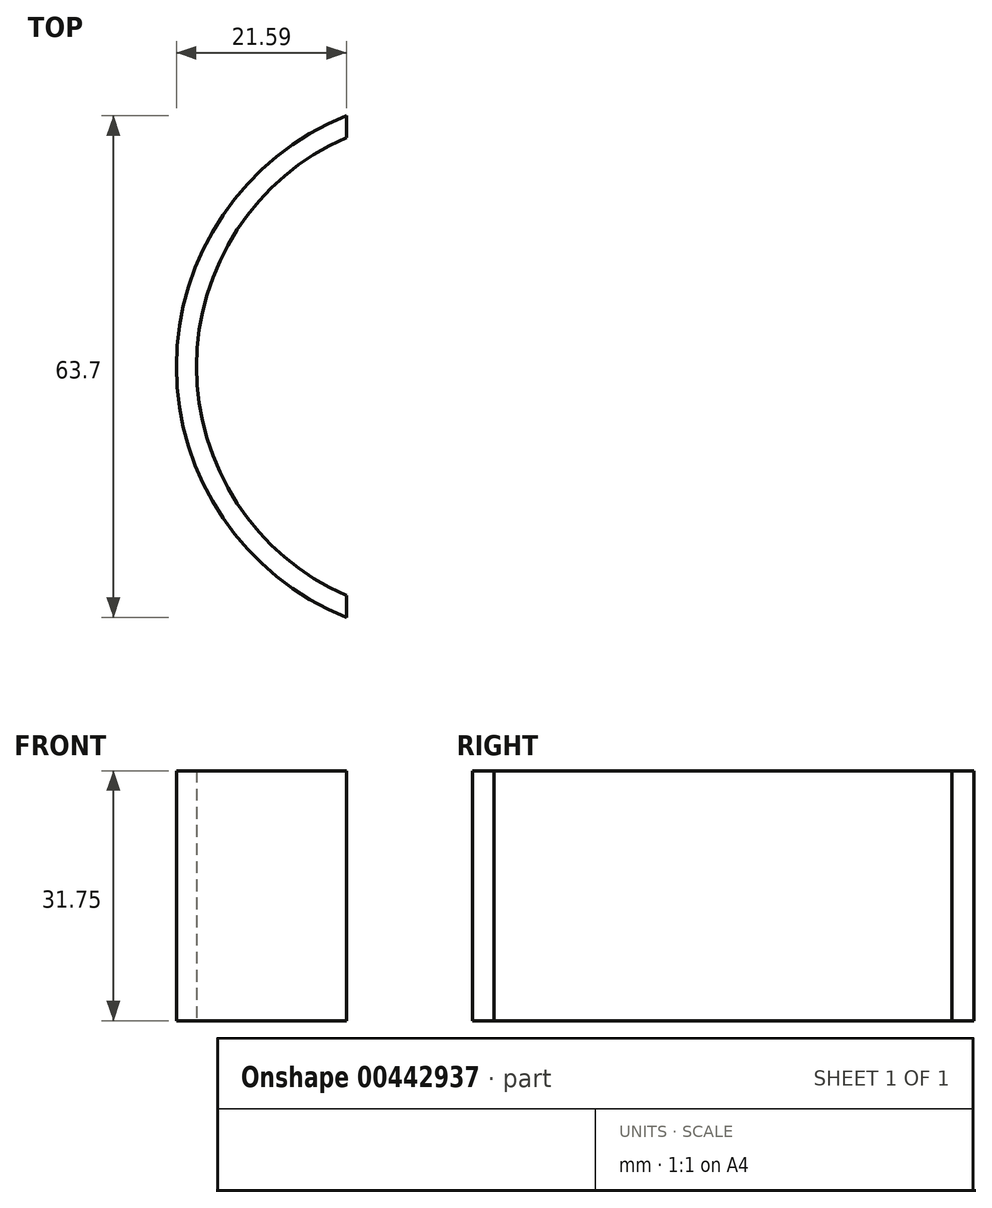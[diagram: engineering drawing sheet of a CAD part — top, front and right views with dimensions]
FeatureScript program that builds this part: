
annotation { "Feature Type Name" : "Feature", "Feature Type Description" : "" }
export const myFeature = defineFeature(function(context is Context, id is Id, definition is map)
    precondition{}
    {
        {
            var Q0;
            Q0=qCreatedBy(makeId("Top.planeOp"),FACE);
            var sketch = newSketch(context, id + "F0", { "sketchPlane" : qUnion([Q0])});
            skArc(sketch, "E0", {"start": v(-12.7, 29.1) * mm, "mid": v(-31.75, 0) * mm, "end": v(-12.7, -29.1) * mm});
            skArc(sketch, "E1", {"start": v(-12.7, 31.85) * mm, "mid": v(-34.3, 0) * mm, "end": v(-12.7, -31.85) * mm});
            skLineSegment(sketch, "E2", {"start": v(-12.7, 29.1) * mm, "end": v(-12.7, 31.85) * mm});
            skLineSegment(sketch, "E3", {"start": v(-12.7, 31.85) * mm, "end": v(-12.7, 29.1) * mm});
            skLineSegment(sketch, "E4.trimOffspring", {"start": v(-12.7, -29.1) * mm, "end": v(-12.7, -31.85) * mm});
            skSolve(sketch);
        }
        {
            var Q0;
            Q0=makeQuery(id+"F0.imprint","IMPRINT",FACE,{"disambiguationData":[TD([[makeQuery(id+"F0.imprint","IMPRINT",EDGE,{"derivedFrom":sQuery(id+"F0.wireOp",EDGE,"E0")}),-1.0]])]});
            extrude(context, id + "F1", {"entities" : qUnion([Q0]), "depth" : 31.75 * mm});
        }
    });
